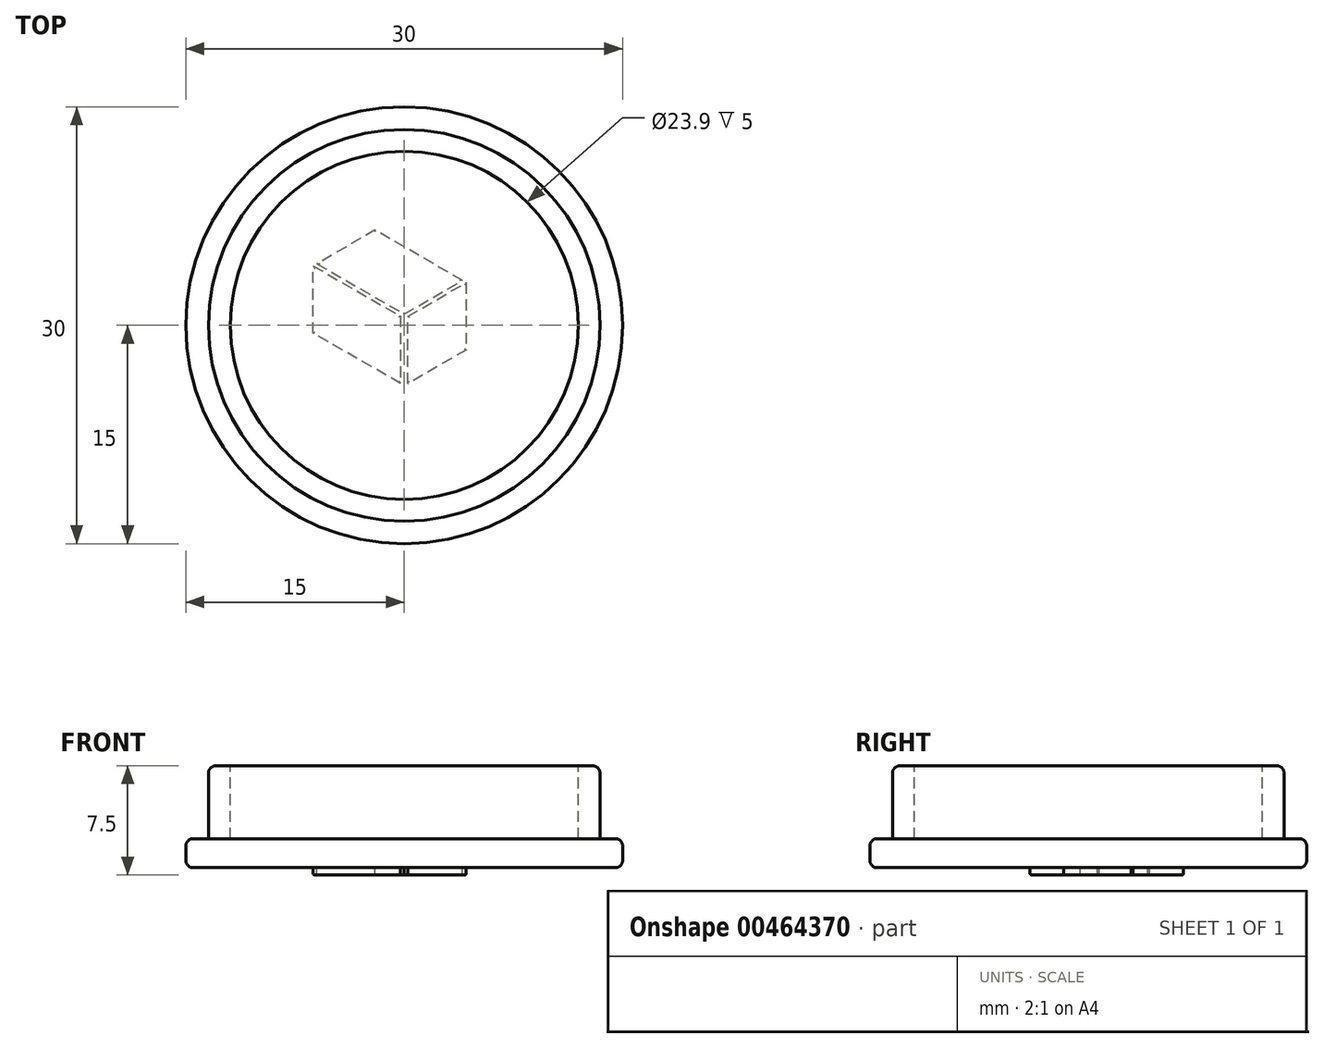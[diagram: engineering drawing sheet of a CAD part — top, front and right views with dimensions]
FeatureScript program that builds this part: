
annotation { "Feature Type Name" : "Feature", "Feature Type Description" : "" }
export const myFeature = defineFeature(function(context is Context, id is Id, definition is map)
    precondition{}
    {
        {
            var Q0;
            Q0=qCreatedBy(makeId("Top.planeOp"),FACE);
            var sketch = newSketch(context, id + "F0", { "sketchPlane" : qUnion([Q0])});
            skCircle(sketch, "E0", {"center": v(0, 0) * mm, "radius": 15 * mm});
            skSolve(sketch);
        }
        {
            var Q0;
            Q0=makeQuery(id+"F0.imprint","IMPRINT",FACE,{"disambiguationData":[TD([[makeQuery(id+"F0.imprint","IMPRINT",EDGE,{"derivedFrom":sQuery(id+"F0.wireOp",EDGE,"E0")}),1.0]])]});
            extrude(context, id + "F1", {"entities" : qUnion([Q0]), "depth" : 2 * mm});
        }
        {
            var Q0;
            Q0=makeQuery(id+"F1.opExtrude","CAP_FACE",FACE,{"disambiguationData":[OSD([sQuery(id+"F0.wireOp",EDGE,"E0")])],"isStart":false});
            var sketch = newSketch(context, id + "F2", { "sketchPlane" : qUnion([Q0])});
            skCircle(sketch, "E1", {"center": v(0, 0) * mm, "radius": 13.45 * mm});
            skSolve(sketch);
        }
        {
            var Q0;
            Q0 = qSketchRegion(id + "F2", true);
            extrude(context, id + "F3", {"entities" : qUnion([Q0]), "operationType" : NewBodyOperationType.ADD, "depth" : 5 * mm});
        }
        {
            var Q0;
            Q0=makeQuery(id+"F1.opExtrude","CAP_EDGE",EDGE,{"disambiguationData":[OSD([sQuery(id+"F0.wireOp",EDGE,"E0")])],"isStart":false});
            var Q1;
            Q1=makeQuery(id+"F3.opExtrude","CAP_EDGE",EDGE,{"disambiguationData":[OSD([sQuery(id+"F2.wireOp",EDGE,"E1")])],"isStart":false});
            var Q2;
            Q2=makeQuery(id+"F1.opExtrude","CAP_EDGE",EDGE,{"disambiguationData":[OSD([sQuery(id+"F0.wireOp",EDGE,"E0")])],"isStart":true});
            fillet(context, id + "F4", {"entities" : qUnion([Q0, Q1, Q2]), "radius" : .5 * mm, "tangentPropagation" : true, "allowEdgeOverflow" : false});
        }
        {
            var Q0;
            Q0=makeQuery(id+"F1.opExtrude","CAP_FACE",FACE,{"disambiguationData":[OSD([sQuery(id+"F0.wireOp",EDGE,"E0")])],"isStart":true});
            var sketch = newSketch(context, id + "F5", { "sketchPlane" : qUnion([Q0])});
            skLineSegment(sketch, "E2", {"start": v(-0.25, -0.62) * mm, "end": v(-0.25, 4) * mm});
            skLineSegment(sketch, "E3", {"start": v(-0.25, 4) * mm, "end": v(-6.25, 0.54) * mm});
            skLineSegment(sketch, "E4", {"start": v(-6.25, 0.54) * mm, "end": v(-6.25, -4.08) * mm});
            skLineSegment(sketch, "E5", {"start": v(-6.25, -4.08) * mm, "end": v(-0.25, -0.62) * mm});
            skLineSegment(sketch, "E6", {"start": v(0.25, -0.62) * mm, "end": v(4.25, -2.93) * mm});
            skLineSegment(sketch, "E7", {"start": v(4.25, -2.93) * mm, "end": v(4.25, 1.7) * mm});
            skLineSegment(sketch, "E8", {"start": v(4.25, 1.7) * mm, "end": v(0.25, 4) * mm});
            skLineSegment(sketch, "E9", {"start": v(0.25, 4) * mm, "end": v(0.25, -0.62) * mm});
            skLineSegment(sketch, "E10", {"start": v(0, -0.76) * mm, "end": v(4, -3.07) * mm});
            skLineSegment(sketch, "E11", {"start": v(4, -3.07) * mm, "end": v(-2, -6.54) * mm});
            skLineSegment(sketch, "E12", {"start": v(-2, -6.54) * mm, "end": v(-6, -4.23) * mm});
            skLineSegment(sketch, "E13", {"start": v(-6, -4.23) * mm, "end": v(0, -0.76) * mm});
            skSolve(sketch);
        }
        {
            var Q0;
            Q0=makeQuery(id+"F5.imprint","IMPRINT",FACE,{"disambiguationData":[TD([[makeQuery(id+"F5.imprint","IMPRINT",EDGE,{"derivedFrom":sQuery(id+"F5.wireOp",EDGE,"E2")}),1.0]])]});
            var Q1;
            Q1=makeQuery(id+"F5.imprint","IMPRINT",FACE,{"disambiguationData":[TD([[makeQuery(id+"F5.imprint","IMPRINT",EDGE,{"derivedFrom":sQuery(id+"F5.wireOp",EDGE,"E6")}),1.0]])]});
            var Q2;
            Q2=makeQuery(id+"F5.imprint","IMPRINT",FACE,{"disambiguationData":[TD([[makeQuery(id+"F5.imprint","IMPRINT",EDGE,{"derivedFrom":sQuery(id+"F5.wireOp",EDGE,"E10")}),-1.0]])]});
            extrude(context, id + "F6", {"entities" : qUnion([Q0, Q1, Q2]), "operationType" : NewBodyOperationType.ADD, "depth" : .5 * mm});
        }
        {
            var Q0;
            Q0=makeQuery(id+"F6.opExtrude","CAP_EDGE",EDGE,{"disambiguationData":[OSD([sQuery(id+"F5.wireOp",EDGE,"E6")])],"isStart":false});
            var Q1;
            Q1=makeQuery(id+"F6.opExtrude","CAP_EDGE",EDGE,{"disambiguationData":[OSD([sQuery(id+"F5.wireOp",EDGE,"E8")])],"isStart":false});
            var Q2;
            Q2=makeQuery(id+"F6.opExtrude","CAP_EDGE",EDGE,{"disambiguationData":[OSD([sQuery(id+"F5.wireOp",EDGE,"E7")])],"isStart":false});
            var Q3;
            Q3=makeQuery(id+"F6.opExtrude","CAP_EDGE",EDGE,{"disambiguationData":[OSD([sQuery(id+"F5.wireOp",EDGE,"E9")])],"isStart":false});
            var Q4;
            Q4=makeQuery(id+"F6.opExtrude","CAP_EDGE",EDGE,{"disambiguationData":[OSD([sQuery(id+"F5.wireOp",EDGE,"E2")])],"isStart":false});
            var Q5;
            Q5=makeQuery(id+"F6.opExtrude","CAP_EDGE",EDGE,{"disambiguationData":[OSD([sQuery(id+"F5.wireOp",EDGE,"E13")])],"isStart":false});
            var Q6;
            Q6=makeQuery(id+"F6.opExtrude","CAP_EDGE",EDGE,{"disambiguationData":[OSD([sQuery(id+"F5.wireOp",EDGE,"E10")])],"isStart":false});
            var Q7;
            Q7=makeQuery(id+"F6.opExtrude","CAP_EDGE",EDGE,{"disambiguationData":[OSD([sQuery(id+"F5.wireOp",EDGE,"E11")])],"isStart":false});
            var Q8;
            Q8=makeQuery(id+"F6.opExtrude","CAP_EDGE",EDGE,{"disambiguationData":[OSD([sQuery(id+"F5.wireOp",EDGE,"E12")])],"isStart":false});
            var Q9;
            Q9=makeQuery(id+"F6.opExtrude","CAP_EDGE",EDGE,{"disambiguationData":[OSD([sQuery(id+"F5.wireOp",EDGE,"E5")])],"isStart":false});
            var Q10;
            Q10=makeQuery(id+"F6.opExtrude","CAP_EDGE",EDGE,{"disambiguationData":[OSD([sQuery(id+"F5.wireOp",EDGE,"E4")])],"isStart":false});
            var Q11;
            Q11=makeQuery(id+"F6.opExtrude","CAP_EDGE",EDGE,{"disambiguationData":[OSD([sQuery(id+"F5.wireOp",EDGE,"E3")])],"isStart":false});
            fillet(context, id + "F7", {"entities" : qUnion([Q0, Q1, Q2, Q3, Q4, Q5, Q6, Q7, Q8, Q9, Q10, Q11]), "radius" : .1 * mm, "tangentPropagation" : true, "allowEdgeOverflow" : false});
        }
        {
            var Q0;
            Q0=makeQuery(id+"F3.opExtrude","CAP_FACE",FACE,{"disambiguationData":[OSD([sQuery(id+"F2.wireOp",EDGE,"E1")])],"isStart":false});
            var sketch = newSketch(context, id + "F8", { "sketchPlane" : qUnion([Q0])});
            skCircle(sketch, "E14", {"center": v(0, 0) * mm, "radius": 11.95 * mm});
            skSolve(sketch);
        }
        {
            var Q0;
            Q0 = qSketchRegion(id + "F8", true);
            extrude(context, id + "F9", {"entities" : qUnion([Q0]), "operationType" : NewBodyOperationType.REMOVE, "oppositeDirection" : true, "depth" : 5 * mm});
        }
    });
